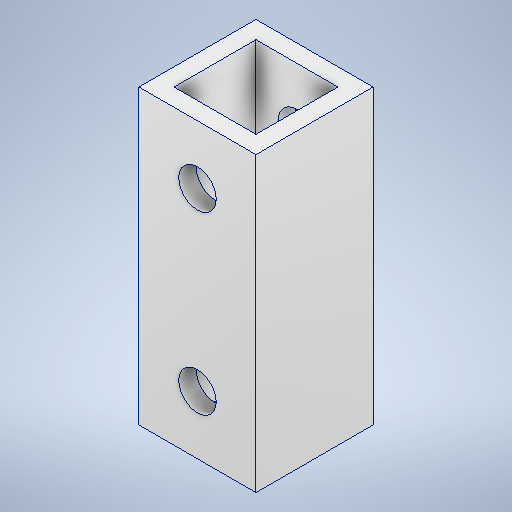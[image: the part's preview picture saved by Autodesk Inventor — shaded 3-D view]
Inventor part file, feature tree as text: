
AUTODESK INVENTOR PART (.ipt)
format: ipt  version: 2025 (Build 290162000, 162)  size: 279,552 bytes
history: native  units: mm
features: sketch x2, other x1, extrude x1, hole x1, mirror x1
ambient origin geometry x8: Origin, YZ Plane, XZ Plane, XY Plane, X Axis, Y Axis, Z Axis, Center Point
bodies: Body1 (feature_tree)
feature tree (6):
  other  "Těleso1"
  extrude  "Vysunutí1"  Depth=10.0mm
  hole  "Díra1"  [1 undecoded]
  mirror  "Zrcadlit1"
  sketch  "Náčrt1"
  sketch  "Náčrt2"
note: 1 required parameter value undecoded (feature->parameter linkage not recoverable at this tier; creation-order binding heuristic only, values carry confidence <= 0.55)
